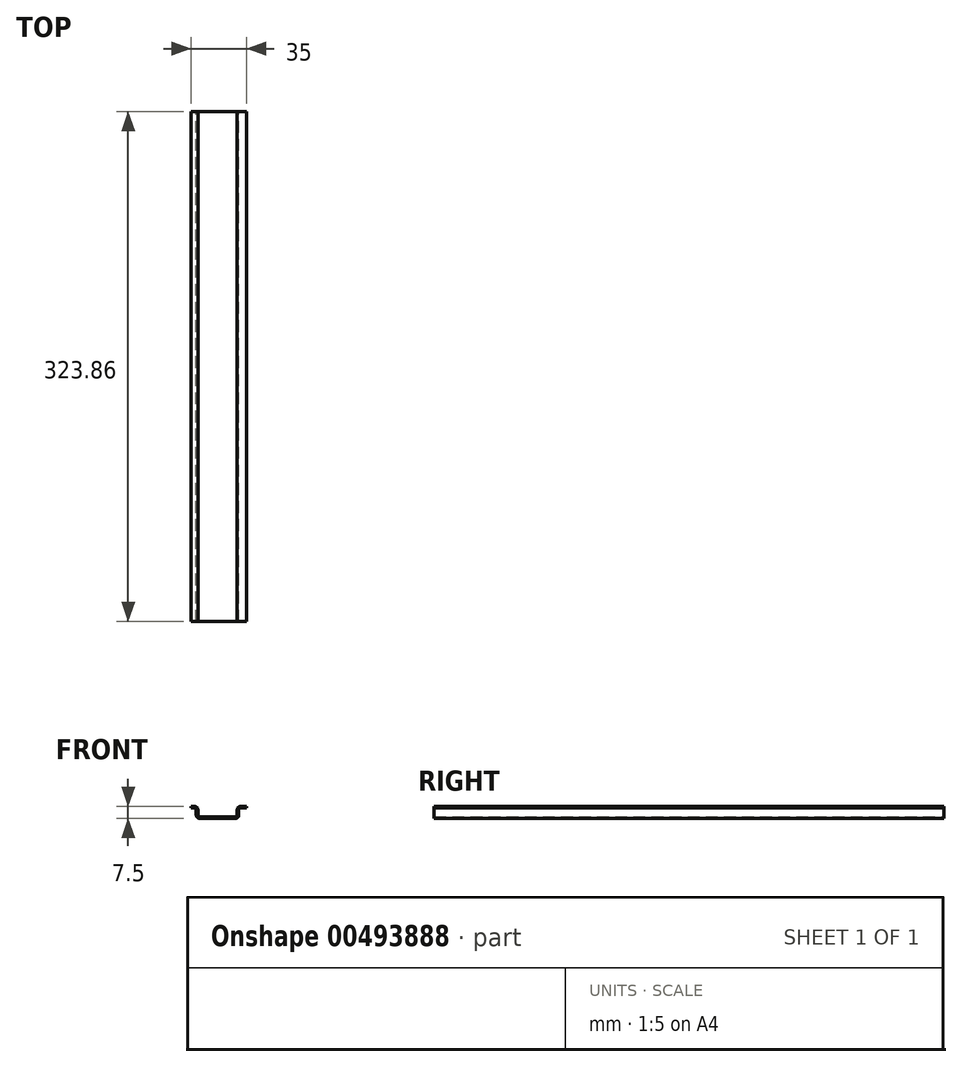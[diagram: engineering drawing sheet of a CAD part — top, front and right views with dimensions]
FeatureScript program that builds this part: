
annotation { "Feature Type Name" : "Feature", "Feature Type Description" : "" }
export const myFeature = defineFeature(function(context is Context, id is Id, definition is map)
    precondition{}
    {
        {
            var Q0;
            Q0=qCreatedBy(makeId("Front.planeOp"),FACE);
            var sketch = newSketch(context, id + "F0", { "sketchPlane" : qUnion([Q0])});
            skLineSegment(sketch, "E0", {"start": v(-11.5, 0) * mm, "end": v(11.5, 0) * mm});
            skLineSegment(sketch, "E1", {"start": v(13.5, 2) * mm, "end": v(13.5, 5.5) * mm});
            skLineSegment(sketch, "E2", {"start": v(14.5, 6.5) * mm, "end": v(18.33, 6.5) * mm});
            skLineSegment(sketch, "E3", {"start": v(18.33, 6.5) * mm, "end": v(18.33, 7.5) * mm});
            skLineSegment(sketch, "E4", {"start": v(18.33, 7.5) * mm, "end": v(14.52, 7.5) * mm});
            skLineSegment(sketch, "E5", {"start": v(12.52, 5.5) * mm, "end": v(12.52, 2) * mm});
            skLineSegment(sketch, "E6", {"start": v(11.52, 1) * mm, "end": v(-11.48, 1) * mm});
            skLineSegment(sketch, "E7", {"start": v(-12.48, 2) * mm, "end": v(-12.48, 5.5) * mm});
            skLineSegment(sketch, "E8", {"start": v(-14.48, 7.5) * mm, "end": v(-16.67, 7.5) * mm});
            skLineSegment(sketch, "E9", {"start": v(-16.67, 7.5) * mm, "end": v(-16.67, 6.5) * mm});
            skLineSegment(sketch, "E10", {"start": v(-16.67, 6.5) * mm, "end": v(-14.5, 6.5) * mm});
            skLineSegment(sketch, "E11", {"start": v(-13.5, 5.5) * mm, "end": v(-13.5, 2) * mm});
            skPoint(sketch, "E12.visualSharp", {"position": v(-12.48, 1) * mm});
            skArc(sketch, "E12.filletArc", {"start": v(-12.48, 2) * mm, "mid": v(-12.2, 1.3) * mm, "end": v(-11.48, 1) * mm});
            skPoint(sketch, "E13.visualSharp", {"position": v(12.52, 1) * mm});
            skArc(sketch, "E13.filletArc", {"start": v(11.52, 1) * mm, "mid": v(12.22, 1.3) * mm, "end": v(12.52, 2) * mm});
            skPoint(sketch, "E14.visualSharp", {"position": v(13.5, 6.5) * mm});
            skArc(sketch, "E14.filletArc", {"start": v(14.5, 6.5) * mm, "mid": v(13.8, 6.2) * mm, "end": v(13.5, 5.5) * mm});
            skPoint(sketch, "E15.visualSharp", {"position": v(-13.5, 6.5) * mm});
            skArc(sketch, "E15.filletArc", {"start": v(-13.5, 5.5) * mm, "mid": v(-13.8, 6.2) * mm, "end": v(-14.5, 6.5) * mm});
            skPoint(sketch, "E16.visualSharp", {"position": v(12.52, 7.5) * mm});
            skArc(sketch, "E16.filletArc", {"start": v(14.52, 7.5) * mm, "mid": v(13.1, 6.92) * mm, "end": v(12.52, 5.5) * mm});
            skPoint(sketch, "E17.visualSharp", {"position": v(13.5, 0) * mm});
            skArc(sketch, "E17.filletArc", {"start": v(11.5, 0) * mm, "mid": v(12.91, 0.59) * mm, "end": v(13.5, 2) * mm});
            skPoint(sketch, "E18.visualSharp", {"position": v(-13.5, 0) * mm});
            skArc(sketch, "E18.filletArc", {"start": v(-13.5, 2) * mm, "mid": v(-12.91, 0.59) * mm, "end": v(-11.5, 0) * mm});
            skPoint(sketch, "E19.visualSharp", {"position": v(-12.48, 7.5) * mm});
            skArc(sketch, "E19.filletArc", {"start": v(-12.48, 5.5) * mm, "mid": v(-13.07, 6.92) * mm, "end": v(-14.48, 7.5) * mm});
            skSolve(sketch);
        }
        {
            var Q0;
            Q0=qSketchRegion(id+"F0",true);
            extrude(context, id + "F1", {"entities" : qUnion([Q0]), "endBound" : BoundingType.SYMMETRIC, "depth" : 323.85 * mm, "offsetDistance" : 25.4 * mm});
        }
    });
